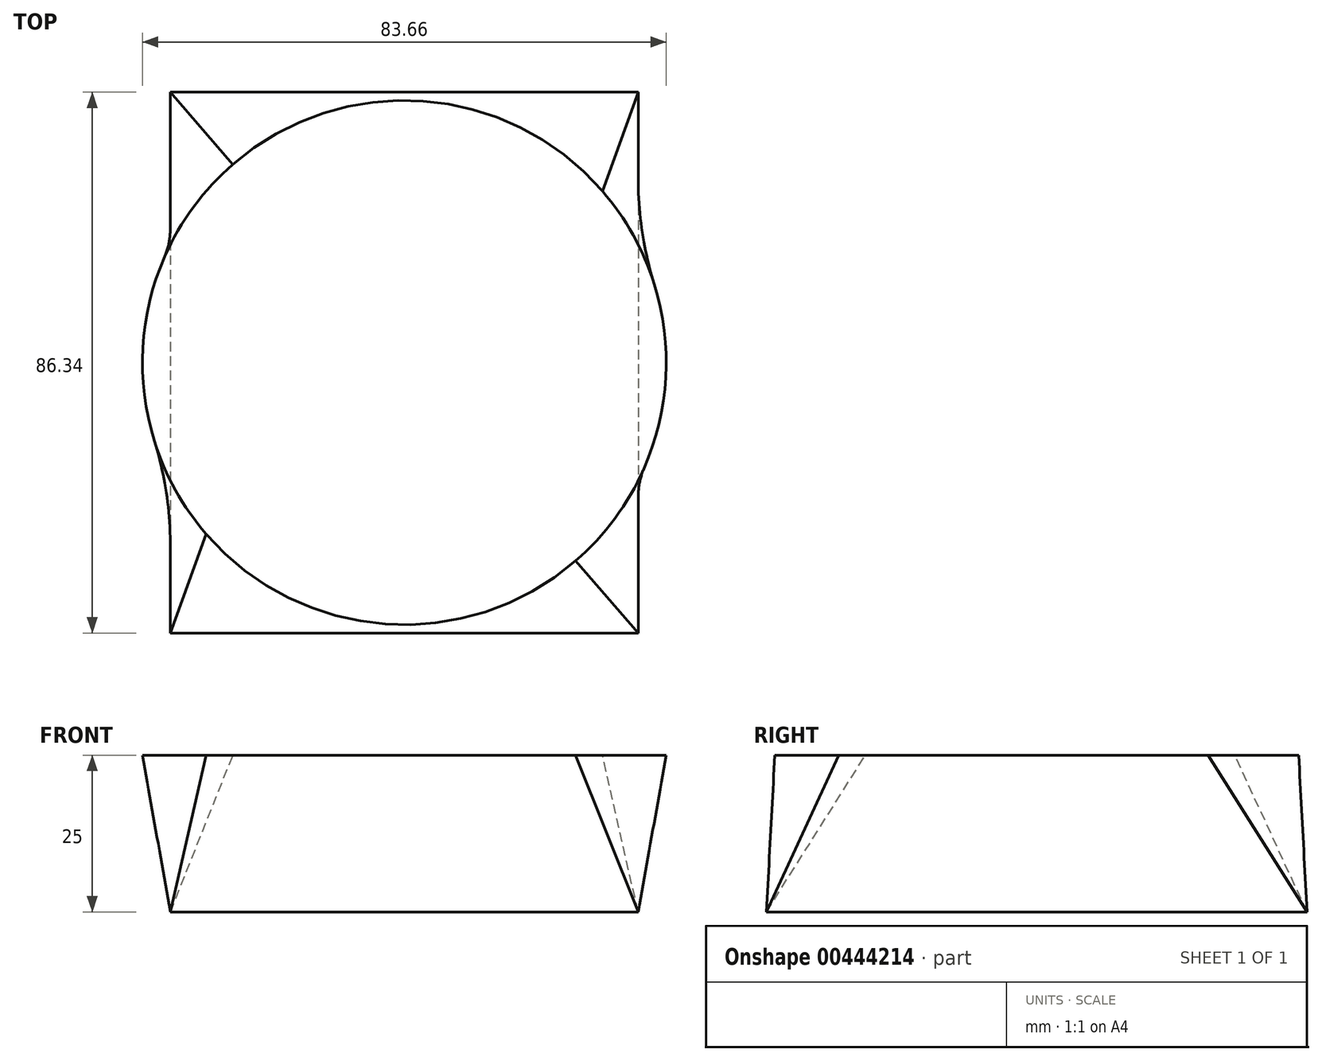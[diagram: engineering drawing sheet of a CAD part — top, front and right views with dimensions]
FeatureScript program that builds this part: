
annotation { "Feature Type Name" : "Feature", "Feature Type Description" : "" }
export const myFeature = defineFeature(function(context is Context, id is Id, definition is map)
    precondition{}
    {
        {
            var Q0;
            Q0=qCreatedBy(makeId("Top.planeOp"),FACE);
            var sketch = newSketch(context, id + "F0", { "sketchPlane" : qUnion([Q0])});
            skLineSegment(sketch, "E0.bottom", {"start": v(-37.35, 43.17) * mm, "end": v(37.35, 43.17) * mm});
            skLineSegment(sketch, "E0.top", {"start": v(-37.35, -43.17) * mm, "end": v(37.35, -43.17) * mm});
            skLineSegment(sketch, "E0.left", {"start": v(-37.35, 43.17) * mm, "end": v(-37.35, -43.17) * mm});
            skLineSegment(sketch, "E0.right", {"start": v(37.35, 43.17) * mm, "end": v(37.35, -43.17) * mm});
            skPoint(sketch, "E0.middle", {"position": v(0, 0) * mm});
            skSolve(sketch);
        }
        {
            var Q0;
            Q0=qCreatedBy(makeId("Top.planeOp"),FACE);
            cPlane(context, id + "F1", {"entities" : qUnion([Q0]), "cplaneType" : CPlaneType.OFFSET, "offset" : 25 * mm, "width" : 150 * mm, "height" : 150 * mm});
        }
        {
            var Q0;
            Q0=qCreatedBy(id+"F1.planeOp",FACE);
            var sketch = newSketch(context, id + "F2", { "sketchPlane" : qUnion([Q0])});
            skCircle(sketch, "E1", {"center": v(0, 0) * mm, "radius": 41.83 * mm});
            skSolve(sketch);
        }
        {
            var Q0;
            Q0=makeQuery(id+"F0.imprint","IMPRINT",FACE,{"disambiguationData":[TD([[makeQuery(id+"F0.imprint","IMPRINT",EDGE,{"derivedFrom":sQuery(id+"F0.wireOp",EDGE,"E0.bottom")}),-1.0]])]});
            var Q1;
            Q1=makeQuery(id+"F2.imprint","IMPRINT",FACE,{"disambiguationData":[TD([[makeQuery(id+"F2.imprint","IMPRINT",EDGE,{"derivedFrom":sQuery(id+"F2.wireOp",EDGE,"E1")}),1.0]])]});
            loft(context, id + "F3", {"sheetProfilesArray" : [{ "sheetProfileEntities" : qUnion([Q0]) }, { "sheetProfileEntities" : qUnion([Q1]) }]});
        }
    });
